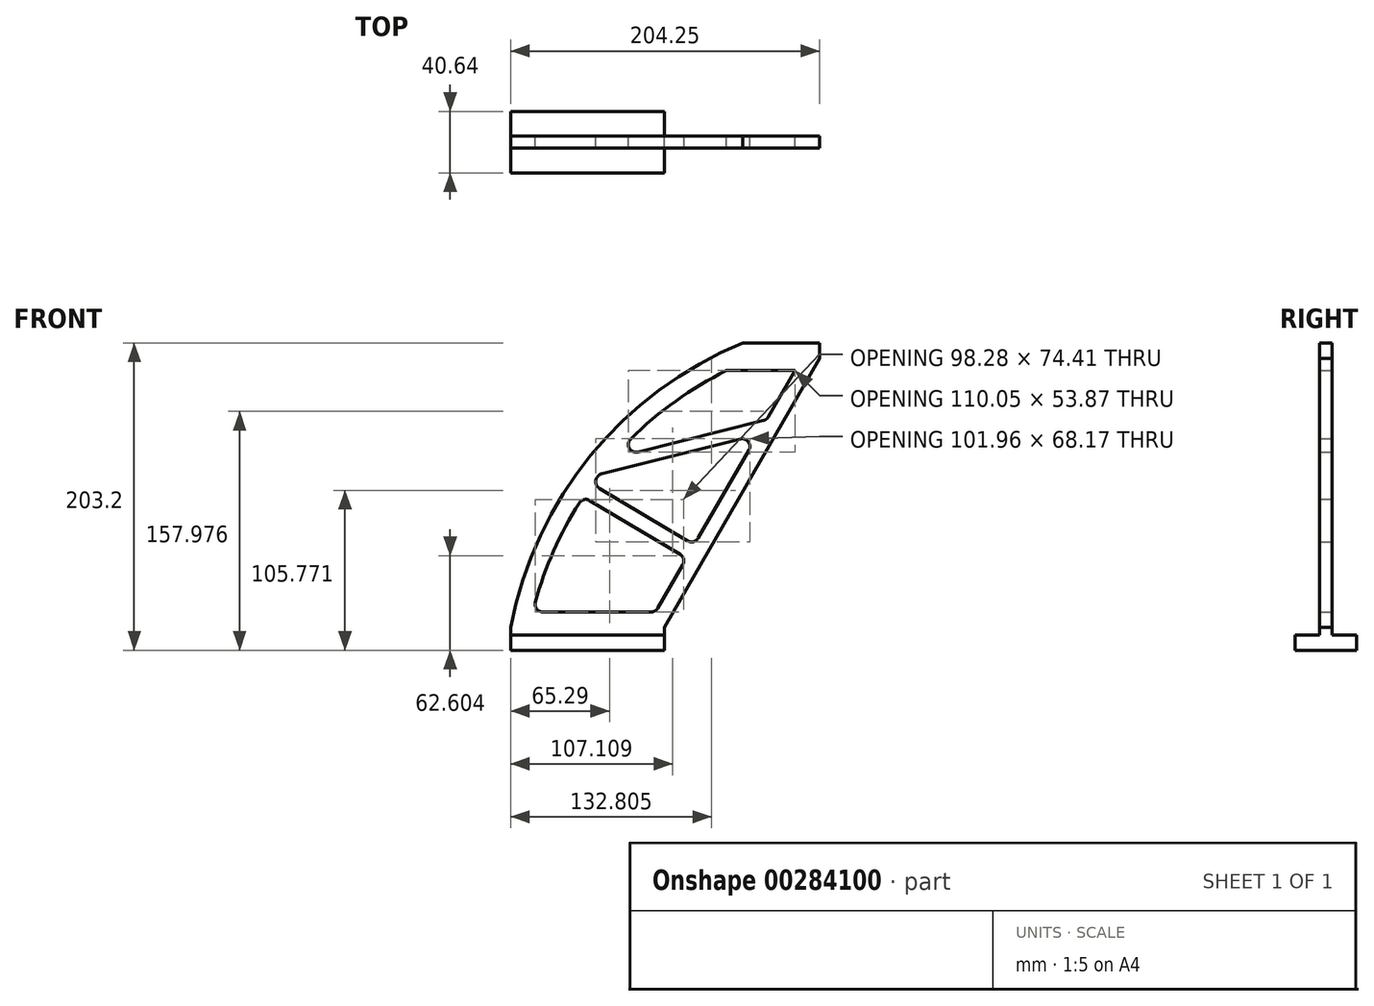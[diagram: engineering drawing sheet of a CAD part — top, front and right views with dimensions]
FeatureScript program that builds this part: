
annotation { "Feature Type Name" : "Feature", "Feature Type Description" : "" }
export const myFeature = defineFeature(function(context is Context, id is Id, definition is map)
    precondition{}
    {
        {
            var Q0;
            Q0=qCreatedBy(makeId("Front.planeOp"),FACE);
            var sketch = newSketch(context, id + "F0", { "sketchPlane" : qUnion([Q0])});
            skLineSegment(sketch, "E0", {"start": v(0, 15.24) * mm, "end": v(0, 0) * mm});
            skLineSegment(sketch, "E1", {"start": v(0, 0) * mm, "end": v(101.6, 0) * mm});
            skLineSegment(sketch, "E2", {"start": v(101.6, 0) * mm, "end": v(101.6, 15.24) * mm});
            skLineSegment(sketch, "E3", {"start": v(101.6, 15.24) * mm, "end": v(204.25, 193.04) * mm});
            skLineSegment(sketch, "E4", {"start": v(204.25, 193.04) * mm, "end": v(204.25, 203.2) * mm});
            skLineSegment(sketch, "E5", {"start": v(204.25, 203.2) * mm, "end": v(153.45, 203.2) * mm});
            skArc(sketch, "E6", {"start": v(153.45, 203.2) * mm, "mid": v(52.83, 128.73) * mm, "end": v(0, 15.24) * mm});
            skLineSegment(sketch, "E7", {"start": v(21.23, 25.4) * mm, "end": v(92.8, 25.4) * mm});
            skLineSegment(sketch, "E8", {"start": v(97.2, 27.94) * mm, "end": v(113.76, 56.62) * mm});
            skLineSegment(sketch, "E9", {"start": v(187.83, 184.91) * mm, "end": v(142.53, 184.91) * mm});
            skArc(sketch, "E10", {"start": v(142.53, 184.91) * mm, "mid": v(109.05, 164.87) * mm, "end": v(79.23, 139.7) * mm});
            skLineSegment(sketch, "E11", {"start": v(166.97, 151.88) * mm, "end": v(84.04, 131.17) * mm});
            skLineSegment(sketch, "E12", {"start": v(52.18, 99.1) * mm, "end": v(111.96, 63.52) * mm});
            skLineSegment(sketch, "E13", {"start": v(151.79, 139.71) * mm, "end": v(60.35, 116.88) * mm});
            skLineSegment(sketch, "E14", {"start": v(58.6, 107.1) * mm, "end": v(116.92, 72.4) * mm});
            skArc(sketch, "E15.trimOffspring", {"start": v(57.55, 115.04) * mm, "mid": v(57.36, 114.79) * mm, "end": v(57.16, 114.54) * mm});
            skArc(sketch, "E16.trimOffspring", {"start": v(45.29, 97.45) * mm, "mid": v(28.36, 65.71) * mm, "end": v(16.33, 31.82) * mm});
            skLineSegment(sketch, "E17.trimOffspring", {"start": v(123.92, 74.22) * mm, "end": v(157.42, 132.24) * mm});
            skLineSegment(sketch, "E18.trimOffspring", {"start": v(170.14, 154.27) * mm, "end": v(187.83, 184.91) * mm});
            skPoint(sketch, "E19.visualSharp", {"position": v(169.06, 152.4) * mm});
            skArc(sketch, "E19.filletArc", {"start": v(166.97, 151.88) * mm, "mid": v(168.8, 152.75) * mm, "end": v(170.14, 154.27) * mm});
            skPoint(sketch, "E20.visualSharp", {"position": v(163.4, 142.61) * mm});
            skArc(sketch, "E20.filletArc", {"start": v(157.42, 132.24) * mm, "mid": v(157.08, 137.84) * mm, "end": v(151.79, 139.71) * mm});
            skPoint(sketch, "E21.visualSharp", {"position": v(121.35, 69.76) * mm});
            skArc(sketch, "E21.filletArc", {"start": v(116.92, 72.4) * mm, "mid": v(120.8, 71.84) * mm, "end": v(123.92, 74.22) * mm});
            skPoint(sketch, "E22.visualSharp", {"position": v(116.26, 60.96) * mm});
            skArc(sketch, "E22.filletArc", {"start": v(113.76, 56.62) * mm, "mid": v(114.27, 60.44) * mm, "end": v(111.96, 63.52) * mm});
            skPoint(sketch, "E23.visualSharp", {"position": v(95.73, 25.4) * mm});
            skArc(sketch, "E23.filletArc", {"start": v(92.8, 25.4) * mm, "mid": v(95.34, 26.08) * mm, "end": v(97.2, 27.94) * mm});
            skPoint(sketch, "E24.visualSharp", {"position": v(14.67, 25.4) * mm});
            skArc(sketch, "E24.filletArc", {"start": v(16.33, 31.82) * mm, "mid": v(17.19, 27.4) * mm, "end": v(21.23, 25.4) * mm});
            skPoint(sketch, "E25.visualSharp", {"position": v(47.97, 101.6) * mm});
            skArc(sketch, "E25.filletArc", {"start": v(52.18, 99.1) * mm, "mid": v(48.4, 99.67) * mm, "end": v(45.29, 97.45) * mm});
            skPoint(sketch, "E26.visualSharp", {"position": v(67.32, 127) * mm});
            skArc(sketch, "E26.filletArc", {"start": v(79.23, 139.7) * mm, "mid": v(78.39, 133.6) * mm, "end": v(84.04, 131.17) * mm});
            skPoint(sketch, "E27.visualSharp", {"position": v(58.64, 116.45) * mm});
            skArc(sketch, "E27.filletArc", {"start": v(60.35, 116.88) * mm, "mid": v(58.8, 116.2) * mm, "end": v(57.55, 115.04) * mm});
            skPoint(sketch, "E28.visualSharp", {"position": v(53.77, 109.97) * mm});
            skArc(sketch, "E28.filletArc", {"start": v(57.16, 114.54) * mm, "mid": v(56.22, 110.5) * mm, "end": v(58.6, 107.1) * mm});
            skLineSegment(sketch, "E29", {"start": v(0, 10.16) * mm, "end": v(101.6, 10.16) * mm});
            skSolve(sketch);
        }
        {
            var Q0;
            {var subQ0=sQuery(id+"F0.wireOp",EDGE,"E3");Q0=makeQuery(id+"F0.imprint","IMPRINT",FACE,{"disambiguationData":[TD([[makeQuery(id+"F0.imprint","IMPRINT",EDGE,{"derivedFrom":subQ0}),1.0]])]});}
            extrude(context, id + "F1", {"entities" : qUnion([Q0]), "depth" : 8.13 * mm, "symmetric" : true});
        }
        {
            var Q0;
            {var subQ0=sQuery(id+"F0.wireOp",EDGE,"E1");Q0=makeQuery(id+"F0.imprint","IMPRINT",FACE,{"disambiguationData":[TD([[makeQuery(id+"F0.imprint","IMPRINT",EDGE,{"derivedFrom":subQ0}),1.0]])]});}
            extrude(context, id + "F2", {"entities" : qUnion([Q0]), "operationType" : NewBodyOperationType.ADD, "depth" : 40.64 * mm, "symmetric" : true});
        }
    });
